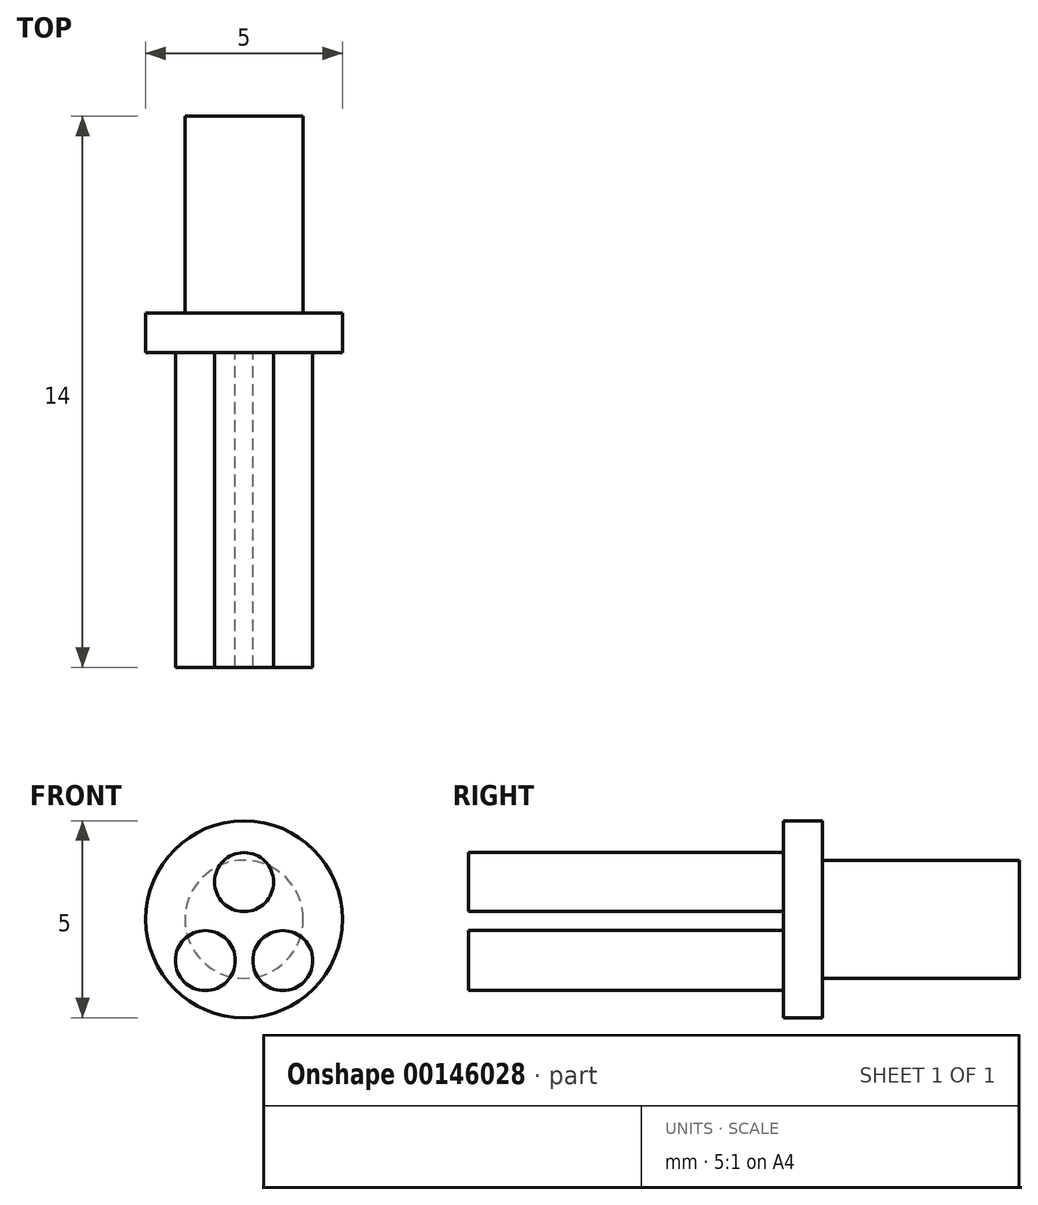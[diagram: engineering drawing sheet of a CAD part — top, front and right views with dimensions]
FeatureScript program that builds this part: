
annotation { "Feature Type Name" : "Feature", "Feature Type Description" : "" }
export const myFeature = defineFeature(function(context is Context, id is Id, definition is map)
    precondition{}
    {
        {
            var Q0;
            Q0=qCreatedBy(makeId("Front.planeOp"),FACE);
            var sketch = newSketch(context, id + "F0", { "sketchPlane" : qUnion([Q0])});
            skCircle(sketch, "E0", {"center": v(0, 0) * mm, "radius": 1.5 * mm});
            skSolve(sketch);
        }
        {
            var Q0;
            Q0 = qSketchRegion(id + "F0", true);
            extrude(context, id + "F1", {"entities" : qUnion([Q0]), "depth" : 5 * mm});
        }
        {
            var Q0;
            Q0=makeQuery(id+"F1.opExtrude","CAP_FACE",FACE,{"disambiguationData":[OSD([sQuery(id+"F0.wireOp",EDGE,"E0")])],"isStart":false});
            var sketch = newSketch(context, id + "F2", { "sketchPlane" : qUnion([Q0])});
            skCircle(sketch, "E1", {"center": v(0, 0) * mm, "radius": 2.5 * mm});
            skSolve(sketch);
        }
        {
            var Q0;
            Q0 = qSketchRegion(id + "F2", true);
            extrude(context, id + "F3", {"entities" : qUnion([Q0]), "operationType" : NewBodyOperationType.ADD, "depth" : 1 * mm});
        }
        {
            var Q0;
            Q0=makeQuery(id+"F3.opExtrude","CAP_FACE",FACE,{"disambiguationData":[OSD([sQuery(id+"F2.wireOp",EDGE,"E1")])],"isStart":false});
            var sketch = newSketch(context, id + "F4", { "sketchPlane" : qUnion([Q0])});
            skCircle(sketch, "E2", {"center": v(0.98, -1.05) * mm, "radius": 0.76 * mm});
            skCircle(sketch, "E3.MirrorC", {"center": v(-0.98, -1.05) * mm, "radius": 0.76 * mm});
            skCircle(sketch, "E4", {"center": v(0, 0.94) * mm, "radius": 0.75 * mm});
            skSolve(sketch);
        }
        {
            var Q0;
            Q0 = qSketchRegion(id + "F4", true);
            extrude(context, id + "F5", {"entities" : qUnion([Q0]), "operationType" : NewBodyOperationType.ADD, "depth" : 8 * mm});
        }
    });
